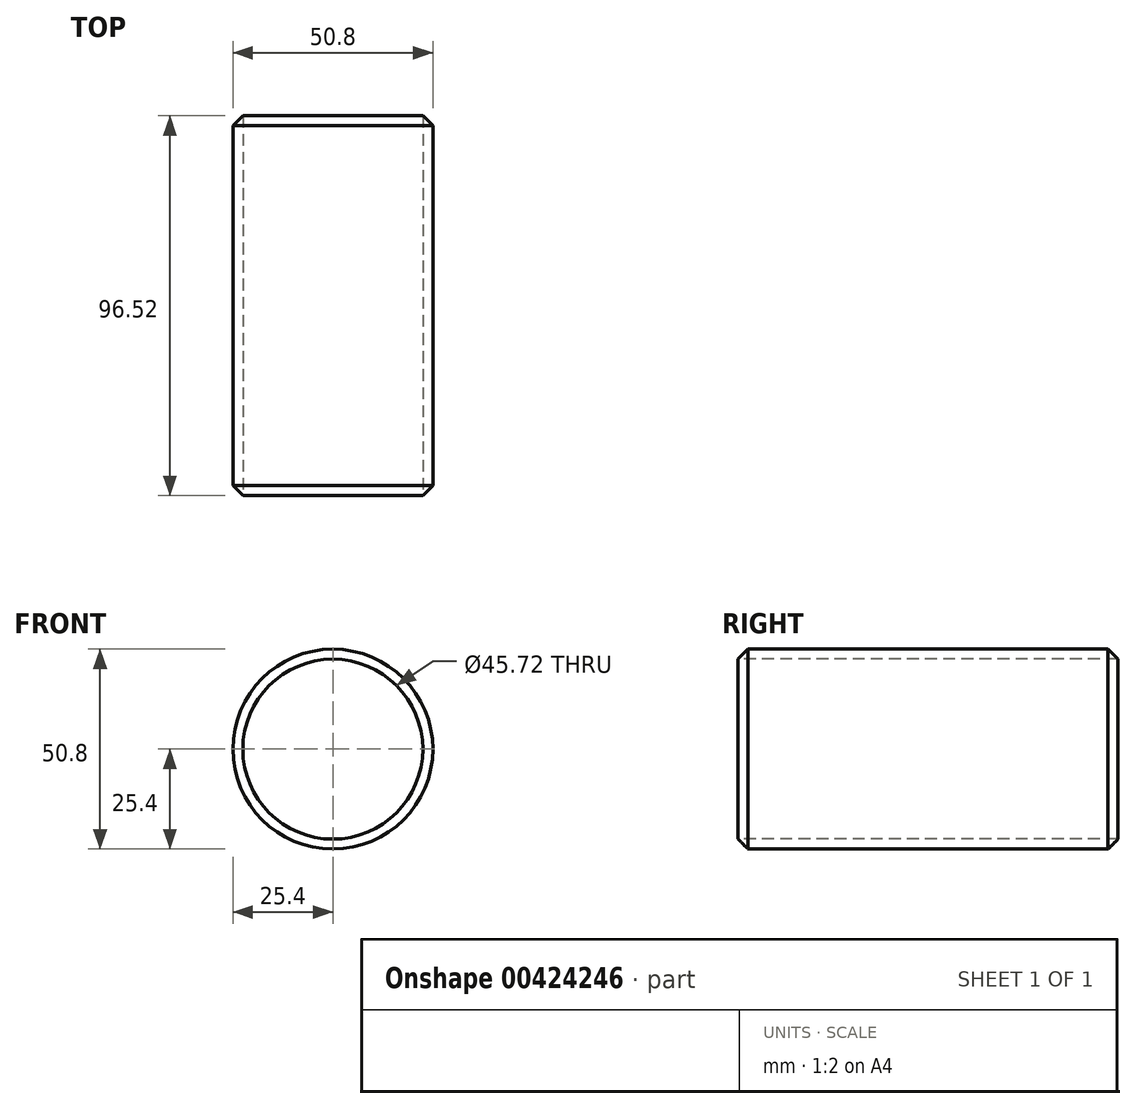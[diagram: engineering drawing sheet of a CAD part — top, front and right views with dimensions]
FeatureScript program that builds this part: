
annotation { "Feature Type Name" : "Feature", "Feature Type Description" : "" }
export const myFeature = defineFeature(function(context is Context, id is Id, definition is map)
    precondition{}
    {
        {
            var Q0;
            Q0=qCreatedBy(makeId("Front.planeOp"),FACE);
            var sketch = newSketch(context, id + "F0", { "sketchPlane" : qUnion([Q0])});
            skCircle(sketch, "E0", {"center": v(0, 0) * mm, "radius": 25.4 * mm});
            skCircle(sketch, "E1", {"center": v(0, 0) * mm, "radius": 23.5 * mm});
            skSolve(sketch);
        }
        {
            var Q0;
            Q0=makeQuery(id+"F0.imprint","IMPRINT",FACE,{"disambiguationData":[TD([[makeQuery(id+"F0.imprint","IMPRINT",EDGE,{"derivedFrom":sQuery(id+"F0.wireOp",EDGE,"E1")}),1.0]])]});
            var Q1;
            Q1=makeQuery(id+"F0.imprint","IMPRINT",FACE,{"disambiguationData":[TD([[makeQuery(id+"F0.imprint","IMPRINT",EDGE,{"derivedFrom":sQuery(id+"F0.wireOp",EDGE,"E0")}),1.0]])]});
            extrude(context, id + "F1", {"entities" : qUnion([Q0, Q1]), "endBound" : BoundingType.SYMMETRIC, "depth" : 101.6 * mm});
        }
        {
            var Q0;
            Q0=makeQuery(id+"F1.opExtrude","CAP_FACE",FACE,{"disambiguationData":[OSD([sQuery(id+"F0.wireOp",EDGE,"E0")])],"isStart":false});
            var sketch = newSketch(context, id + "F2", { "sketchPlane" : qUnion([Q0])});
            skLineSegment(sketch, "E2", {"start": v(-25.4, 0) * mm, "end": v(25.4, 0) * mm, "construction": true});
            skLineSegment(sketch, "E3", {"start": v(4.03, 25.08) * mm, "end": v(-5.49, -24.8) * mm, "construction": true});
            skPoint(sketch, "E4", {"position": v(0, 0) * mm});
            skSolve(sketch);
        }
        {
            var Q0;
            Q0=sQuery(id+"F2.wireOp",VERTEX,"E4");
            var Q1;
            Q1=makeQuery(id+"F1.opExtrude","SWEPT_BODY",BODY,{"disambiguationData":[OSD([sQuery(id+"F0.wireOp",EDGE,"E0")])]});
            hole(context, id + "F3", {"style" : HoleStyle.SIMPLE, "endStyle" : HoleEndStyle.THROUGH, "holeDiameter" : 45.72 * mm, "isTappedThrough" : true, "tappedDepth" : 12.7 * mm, "tapClearance" : 3, "locations" : qUnion([Q0]), "scope" : qUnion([Q1])});
        }
        {
            var Q0;
            Q0=makeQuery(id+"F1.opExtrude","SWEPT_FACE",FACE,{"disambiguationData":[OSD([sQuery(id+"F0.wireOp",EDGE,"E0")])]});
            chamfer(context, id + "F4", {"entities" : qUnion([Q0]), "width" : 5.08 * mm, "tangentPropagation" : true});
        }
    });
